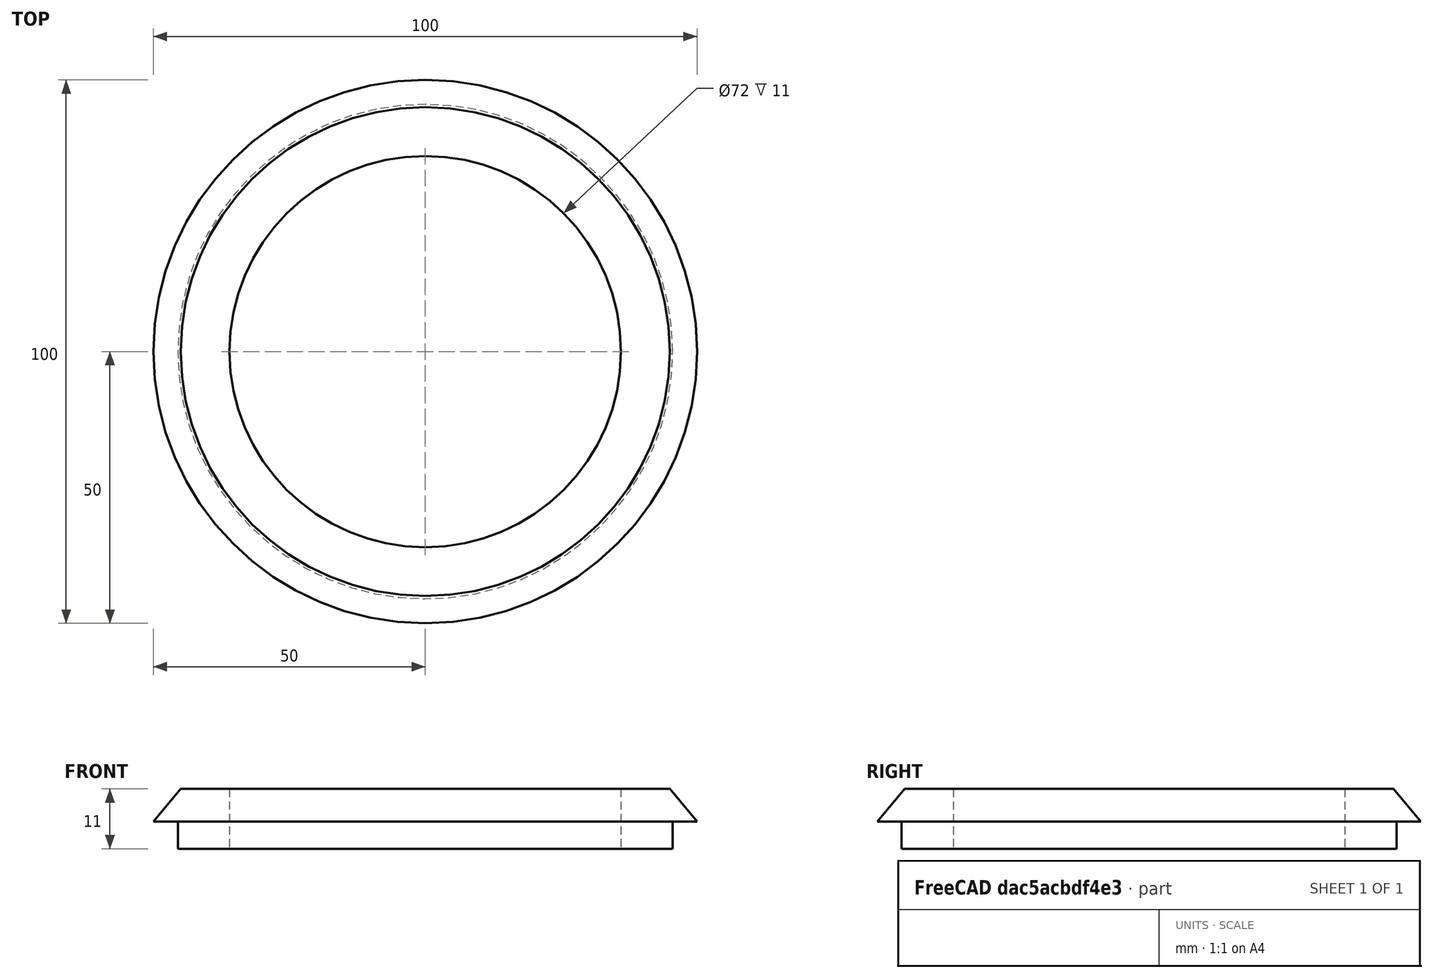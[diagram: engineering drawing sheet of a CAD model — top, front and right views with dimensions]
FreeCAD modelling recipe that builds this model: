
FCSTD DOCUMENT  (FreeCAD 1.0R1.0.1)
Label: camgear_slider
License: All rights reserved
LicenseURL: http://en.wikipedia.org/wiki/All_rights_reserved
objects: Sketcher::SketchObject×1, Part::Revolution×1
note: 3 computed .brp shape members not serialized (recipe doc carries the construction recipe); baked Part::Feature solids carry a one-line shape summary decoded from their .brp

FEATURE [Sketcher::SketchObject] Sketch
  ArcFitTolerance = 1e-06
  FullyConstrained = false
  MakeInternals = false
  Placement = pos=(0,0,0) rot=(1,0,0;1.5708rad)
  sketch-geometry (6):
    g0: LineSegment StartX=36 StartY=0 StartZ=0 EndX=45.5 EndY=0 EndZ=0
    g1: LineSegment StartX=45.5 StartY=0 StartZ=0 EndX=45.5 EndY=5 EndZ=0
    g2: LineSegment StartX=45.5 StartY=5 StartZ=0 EndX=50 EndY=5 EndZ=0
    g3: LineSegment StartX=50 StartY=5 StartZ=0 EndX=44.9831 EndY=11 EndZ=0
    g4: LineSegment StartX=44.9831 StartY=11 StartZ=0 EndX=36 EndY=11 EndZ=0
    g5: LineSegment StartX=36 StartY=11 StartZ=0 EndX=36 EndY=0 EndZ=0
  constraints (17):
    c: PointOnObject(g0,g-1)
    c: PointOnObject(g0,g-1)
    c: Coincident(g0,g1)
    c: Vertical(g1)
    c: Coincident(g1,g2)
    c: Horizontal(g2)
    c: Coincident(g2,g3)
    c: Coincident(g3,g4)
    c: Horizontal(g4)
    c: Coincident(g4,g5)
    c: Coincident(g5,g0)
    c: Vertical(g5)
    c: DistanceX(g-1,g0) = 36
    c: DistanceX(g-1,g0) = 45.5
    c: DistanceY(g1,g1) = 5
    c: DistanceY(g5,g5) = 11
    c: Distance(g2,g-2) = 50
FEATURE [Part::Revolution] Revolve
  Angle = 360
  Axis = (0,0,1)
  Base = (0,0,0)
  FaceMakerClass = Part::FaceMakerBullseye
  Solid = true
  Source = -> Sketch
  Symmetric = false
